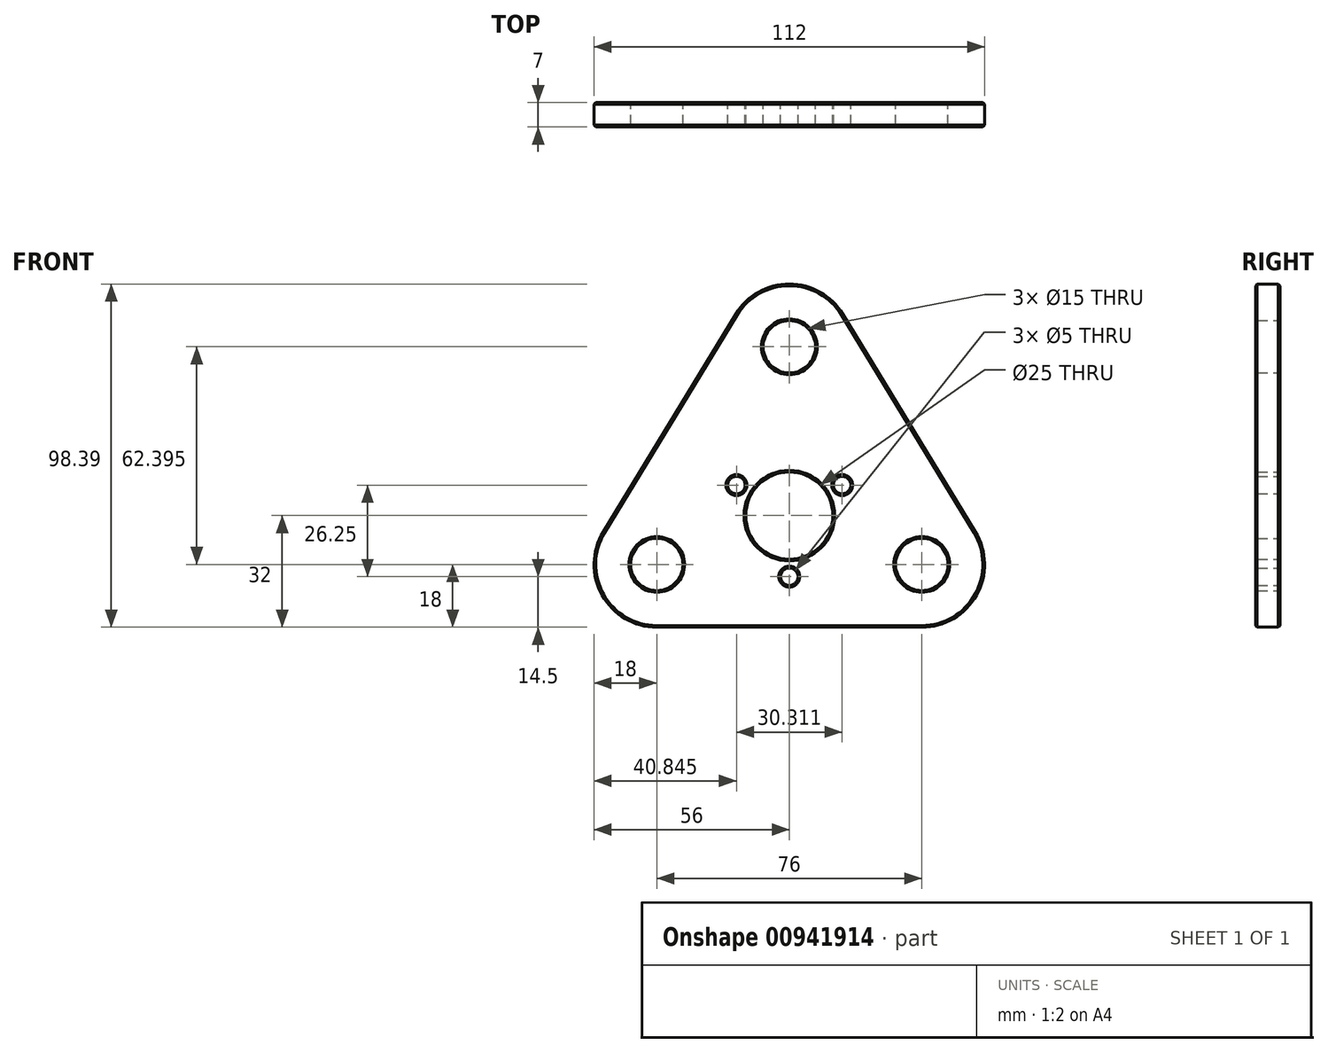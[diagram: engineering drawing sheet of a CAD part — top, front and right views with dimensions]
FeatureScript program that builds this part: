
annotation { "Feature Type Name" : "Feature", "Feature Type Description" : "" }
export const myFeature = defineFeature(function(context is Context, id is Id, definition is map)
    precondition{}
    {
        {
            var Q0;
            Q0=qCreatedBy(makeId("Front.planeOp"),FACE);
            var sketch = newSketch(context, id + "F0", { "sketchPlane" : qUnion([Q0])});
            skLineSegment(sketch, "E0", {"start": v(-38, -32) * mm, "end": v(38, -32) * mm});
            skLineSegment(sketch, "E1", {"start": v(53.37, -4.64) * mm, "end": v(15.37, 57.76) * mm});
            skLineSegment(sketch, "E2", {"start": v(-15.37, 57.76) * mm, "end": v(-53.37, -4.64) * mm});
            skPoint(sketch, "E3.visualSharp", {"position": v(0, 83) * mm});
            skArc(sketch, "E3.filletArc", {"start": v(15.37, 57.76) * mm, "mid": v(0, 66.4) * mm, "end": v(-15.37, 57.76) * mm});
            skPoint(sketch, "E4.visualSharp", {"position": v(70.04, -32) * mm});
            skArc(sketch, "E4.filletArc", {"start": v(38, -32) * mm, "mid": v(53.7, -22.82) * mm, "end": v(53.37, -4.64) * mm});
            skPoint(sketch, "E5.visualSharp", {"position": v(-70.04, -32) * mm});
            skArc(sketch, "E5.filletArc", {"start": v(-53.37, -4.64) * mm, "mid": v(-53.7, -22.82) * mm, "end": v(-38, -32) * mm});
            skCircle(sketch, "E6", {"center": v(0, 48.4) * mm, "radius": 7.5 * mm});
            skCircle(sketch, "E7", {"center": v(-38, -14) * mm, "radius": 7.5 * mm});
            skCircle(sketch, "E8", {"center": v(38, -14) * mm, "radius": 7.5 * mm});
            skCircle(sketch, "E9", {"center": v(0, 0) * mm, "radius": 12.5 * mm});
            skCircle(sketch, "E10", {"center": v(0, 0) * mm, "radius": 17.5 * mm, "construction": true});
            skLineSegment(sketch, "E11", {"start": v(0, 0) * mm, "end": v(-15.16, 8.75) * mm, "construction": true});
            skLineSegment(sketch, "E12", {"start": v(0, 0) * mm, "end": v(15.16, 8.75) * mm, "construction": true});
            skPoint(sketch, "E13", {"position": v(0, -17.5) * mm});
            skSolve(sketch);
        }
        {
            var Q0;
            Q0 = qSketchRegion(id + "F0", true);
            extrude(context, id + "F1", {"entities" : qUnion([Q0]), "depth" : 7 * mm, "offsetDistance" : 25 * mm});
        }
        {
            var Q0;
            Q0=makeQuery(id+"F1.opExtrude","CAP_FACE",FACE,{"disambiguationData":[OSD([sQuery(id+"F0.wireOp",EDGE,"E0"),sQuery(id+"F0.wireOp",EDGE,"E1"),sQuery(id+"F0.wireOp",EDGE,"E2"),sQuery(id+"F0.wireOp",EDGE,"E3.filletArc"),sQuery(id+"F0.wireOp",EDGE,"E4.filletArc"),sQuery(id+"F0.wireOp",EDGE,"E5.filletArc"),sQuery(id+"F0.wireOp",EDGE,"E6"),sQuery(id+"F0.wireOp",EDGE,"E7"),sQuery(id+"F0.wireOp",EDGE,"E8"),sQuery(id+"F0.wireOp",EDGE,"E9")])],"isStart":false});
            var sketch = newSketch(context, id + "F2", { "sketchPlane" : qUnion([Q0])});
            skPoint(sketch, "E14.0", {"position": v(-15.16, 8.75) * mm});
            skPoint(sketch, "E14.1", {"position": v(0, -17.5) * mm});
            skPoint(sketch, "E14.2", {"position": v(15.16, 8.75) * mm});
            skSolve(sketch);
        }
        {
            var Q0;
            Q0=sQuery(id+"F2.wireOp",VERTEX,"E14.0");
            var Q1;
            Q1=sQuery(id+"F2.wireOp",VERTEX,"E14.2");
            var Q2;
            Q2=sQuery(id+"F2.wireOp",VERTEX,"E14.1");
            var Q3;
            Q3=makeQuery(id+"F1.opExtrude","SWEPT_BODY",BODY,{"disambiguationData":[OSD([sQuery(id+"F0.wireOp",EDGE,"E0"),sQuery(id+"F0.wireOp",EDGE,"E1"),sQuery(id+"F0.wireOp",EDGE,"E2"),sQuery(id+"F0.wireOp",EDGE,"E3.filletArc"),sQuery(id+"F0.wireOp",EDGE,"E4.filletArc"),sQuery(id+"F0.wireOp",EDGE,"E5.filletArc"),sQuery(id+"F0.wireOp",EDGE,"E6"),sQuery(id+"F0.wireOp",EDGE,"E7"),sQuery(id+"F0.wireOp",EDGE,"E8"),sQuery(id+"F0.wireOp",EDGE,"E9")])]});
            hole(context, id + "F3", {"style" : HoleStyle.SIMPLE, "endStyle" : HoleEndStyle.THROUGH, "standardTappedOrClearance" : lookupTablePath({ "standard" : "ISO", "engagement" : "75%", "pitch" : "1 mm", "size" : "M6", "type" : "Tapped" }), "standardBlindInLast" : lookupTablePath({ "standard" : "ISO", "fit" : "Normal", "engagement" : "75%", "pitch" : "1 mm", "size" : "M6", "type" : "Clearance & tapped" }), "holeDiameter" : 5 * mm, "majorDiameter" : 6 * mm, "showTappedDepth" : true, "isTappedThrough" : true, "tappedDepth" : 15 * mm, "tapClearance" : 3, "startFromSketch" : true, "locations" : qUnion([Q0, Q1, Q2]), "scope" : qUnion([Q3])});
        }
        {
            var Q0;
            Q0=makeQuery(id+"F1.opExtrude","CAP_FACE",FACE,{"disambiguationData":[OSD([sQuery(id+"F0.wireOp",EDGE,"E0"),sQuery(id+"F0.wireOp",EDGE,"E1"),sQuery(id+"F0.wireOp",EDGE,"E2"),sQuery(id+"F0.wireOp",EDGE,"E3.filletArc"),sQuery(id+"F0.wireOp",EDGE,"E4.filletArc"),sQuery(id+"F0.wireOp",EDGE,"E5.filletArc"),sQuery(id+"F0.wireOp",EDGE,"E6"),sQuery(id+"F0.wireOp",EDGE,"E7"),sQuery(id+"F0.wireOp",EDGE,"E8"),sQuery(id+"F0.wireOp",EDGE,"E9"),sQuery(id+"F0.wireOp",EDGE,"EbIFcVGW-qfQ5-f0hh-bYaB-UIWmjxN4vp9O"),sQuery(id+"F0.wireOp",EDGE,"tUE3wfjz-mUNx-Vc7V-SR3N-g8dKb8yFtn6o"),sQuery(id+"F0.wireOp",EDGE,"HPJGAJ8k-gcWm-KseC-X1Br-1BvLGVH0XyRt")])],"isStart":false});
            var Q1;
            Q1=makeQuery(id+"F1.opExtrude","CAP_FACE",FACE,{"disambiguationData":[OSD([sQuery(id+"F0.wireOp",EDGE,"E0"),sQuery(id+"F0.wireOp",EDGE,"E1"),sQuery(id+"F0.wireOp",EDGE,"E2"),sQuery(id+"F0.wireOp",EDGE,"E3.filletArc"),sQuery(id+"F0.wireOp",EDGE,"E4.filletArc"),sQuery(id+"F0.wireOp",EDGE,"E5.filletArc"),sQuery(id+"F0.wireOp",EDGE,"E6"),sQuery(id+"F0.wireOp",EDGE,"E7"),sQuery(id+"F0.wireOp",EDGE,"E8"),sQuery(id+"F0.wireOp",EDGE,"E9"),sQuery(id+"F0.wireOp",EDGE,"EbIFcVGW-qfQ5-f0hh-bYaB-UIWmjxN4vp9O"),sQuery(id+"F0.wireOp",EDGE,"tUE3wfjz-mUNx-Vc7V-SR3N-g8dKb8yFtn6o"),sQuery(id+"F0.wireOp",EDGE,"HPJGAJ8k-gcWm-KseC-X1Br-1BvLGVH0XyRt")])],"isStart":true});
            chamfer(context, id + "F4", {"entities" : qUnion([Q0, Q1]), "width" : 0.5 * mm, "tangentPropagation" : true});
        }
    });
